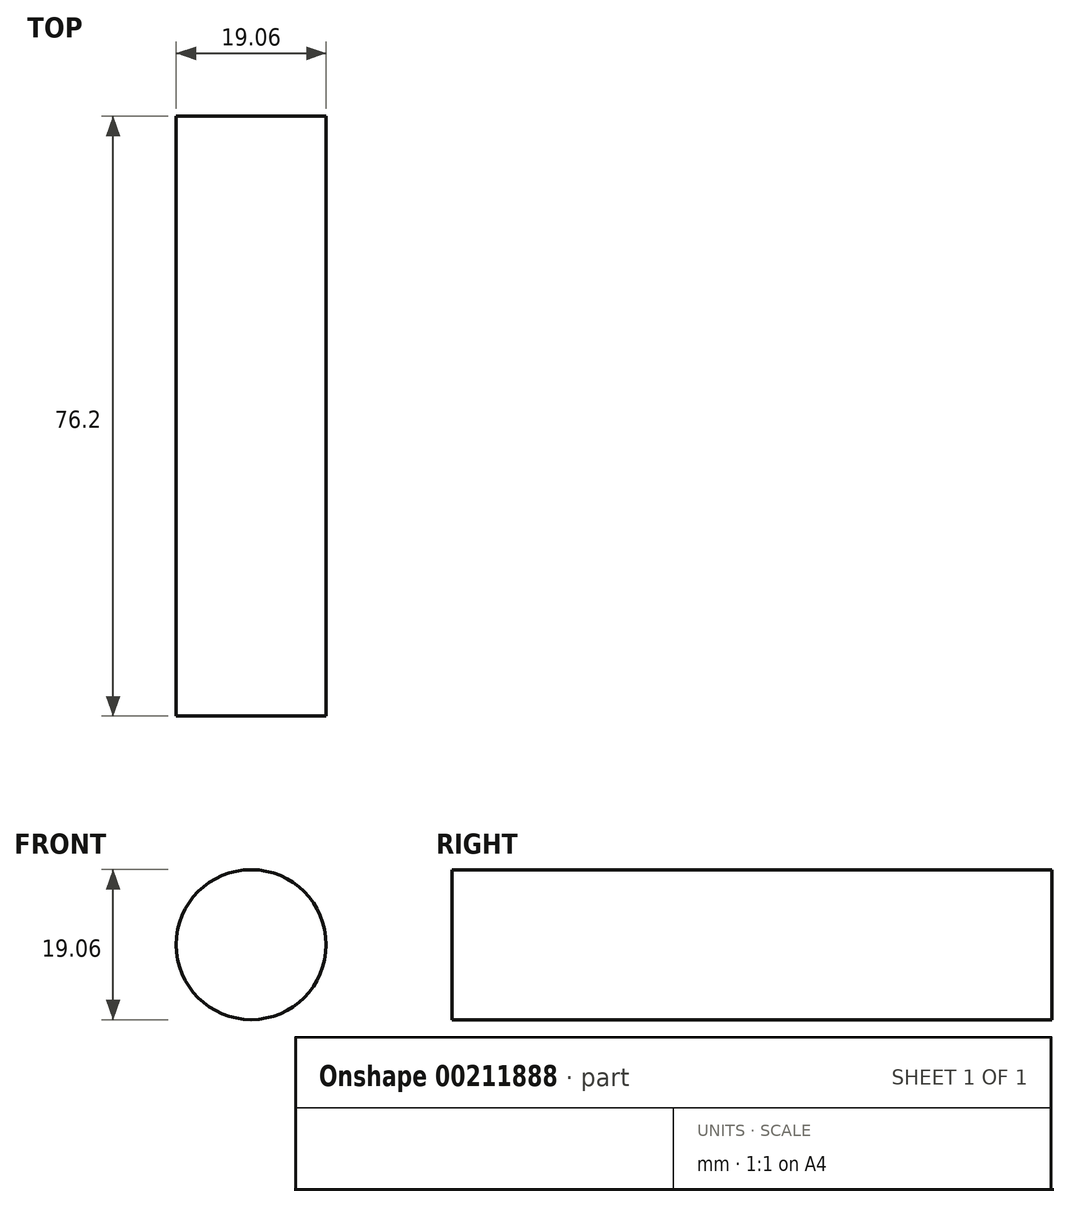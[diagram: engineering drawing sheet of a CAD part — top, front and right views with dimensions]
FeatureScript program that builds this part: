
annotation { "Feature Type Name" : "Feature", "Feature Type Description" : "" }
export const myFeature = defineFeature(function(context is Context, id is Id, definition is map)
    precondition{}
    {
        {
            var Q0;
            Q0=qCreatedBy(makeId("Front.planeOp"),FACE);
            var sketch = newSketch(context, id + "F0", { "sketchPlane" : qUnion([Q0])});
            skCircle(sketch, "E0", {"center": v(0, 0) * mm, "radius": 9.53 * mm});
            skSolve(sketch);
        }
        {
            var Q0;
            Q0 = qSketchRegion(id + "F0", true);
            extrude(context, id + "F1", {"entities" : qUnion([Q0]), "endBound" : BoundingType.SYMMETRIC, "depth" : 76.2 * mm});
        }
    });
